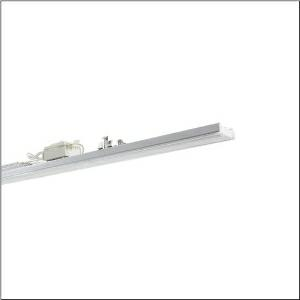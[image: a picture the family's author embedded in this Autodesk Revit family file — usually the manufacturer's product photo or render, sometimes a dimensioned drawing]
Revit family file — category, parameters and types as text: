
# Revit family: licross_11_recessed_mo_51tl11mn4axg
name_source: partatom
category: Lighting Fixtures
units: mm (PartAtom-declared; Revit-internal decimal feet)

## family parameters
Cut with Voids When Loaded = No
Host = Face
Light Source = No
Part Type = Normal
Room Calculation Point = No
Round Connector Dimension = Use Diameter
Shared = No

## types (1)
- --- (1 x LED, 10130 lm, 55.2 W, 4000K)
    Apparent Load = 55 VA
    CIE Flux Codes = 89 96 99 100 100
    Color Rendering = 80
    Color Temperature = 4000K
    Default Elevation = 1800 mm
    Description = Licross 11 Recessed MO, luminaire insert, of sheet steel, coil coated, white, length: 1.500mm, width: 66mm, height: 67mm, LED rated luminous flux: 10.130lm, light colour: 840, SDCM (Standard Deviation of Colour Matching)MacAdam ≤ 2 SDCM (initial), control gear: ON/OFF Multilumen, with plug, 3-pole, with phase selection, mains connection: 220..240V, AC, 50/60Hz, rated input power: 55W, internal wiring halogen-free, primary light control with lens, of plastic, primary optical cover: cover, of PMMA, light emission: direct distribution, primary light characteristic: symmetric, protection rating (complete): IP40, insulation class (complete): insulation class I (protective earthing), certification: CE, ENEC, VDE, UKCA, protection symbol: D if used in an environment without relevant dust loads with corresponding accessories, impact resistance: IK06, permissible ambient temperature for indoor applications: -35..+40°C, corresponds to IFS (International Featured Standards) requirements for safety and quality in the food industry, reducing of maximum allowable ambient temperature of 5°C with ceiling mounting, The light source and the operating device comply with the requirements of the Ecodesign Regulation (EU) 2019/2020 and are replaceable in accordance with this regulation, packaging unit: 1 piece
    Height = 58 mm
    Lamp = 1 x LED
    Lamp Light Flux = 10130 lm
    Lamp Power = 55.2 W
    Lamp count = 1
    Length = 1500 mm
    Luminous efficacy = 184 lm/W
    Manufacturer = Siteco
    ModVariant = No
    Model = 51TL11MN4AXG
    Mounting Place = Ceiling
    Mounting Type = Pendant
    Number of Poles = 1
    OnlyDefault = Yes
    Power Factor = 1
    Product Name = Licross 11 Recessed MO
    Product group = luminaire insert | ceiling pendant
    ProductGroupID = 901
    Protection Class = Protection class I
    Protection Degree = IP 40
    RLX_Detail_Level = 1
    RLX_Emergency_Light_Flux = 0 lm
    RLX_Emergency_Type = 0
    RLX_Emergency_Type_DB = No
    RlxData = <blob elided: 22429 chars, md5=2a4cbcc1>
    Socket = socket
    Standby Power = 0 W
    System Light Flux = 10130 lm
    System Power = 55 W
    Type Comments = factory setting: luminous flux: 100 % | (A | C | E) | 126 mA
    Type Image = l_1296930.jpg
    URL = http://relux.com
    VarID = @adj_089451
    Voltage = 0 V
    Weight = 0.00 kg
    Width = 66 mm

## geometry (parser evidence)
native form markers: Blend x4, Sweep x9
no freeform markers — native parametric forms only
